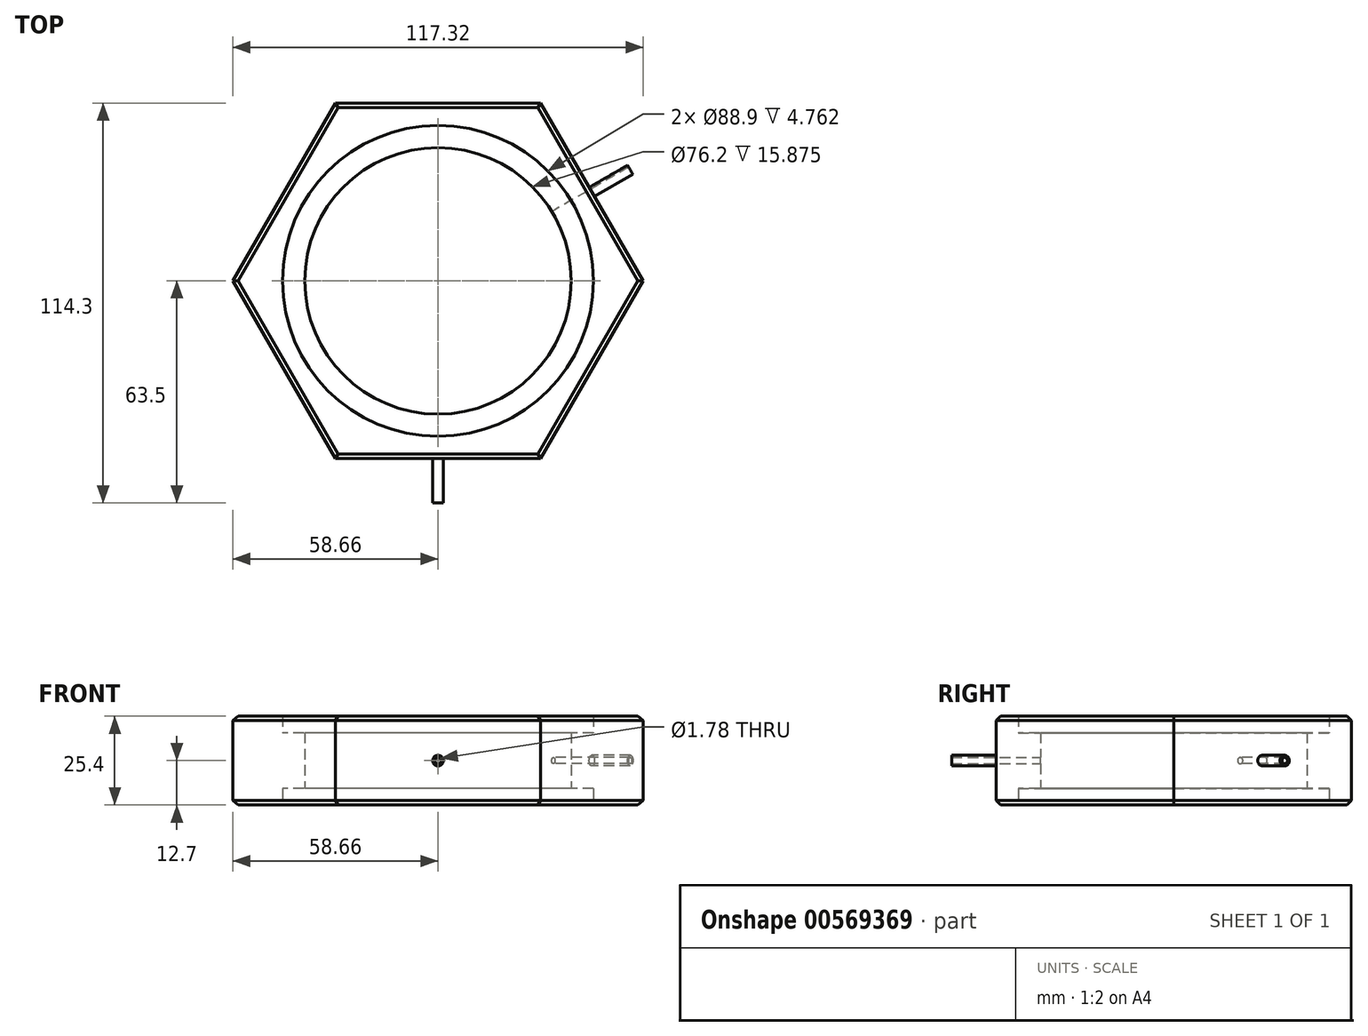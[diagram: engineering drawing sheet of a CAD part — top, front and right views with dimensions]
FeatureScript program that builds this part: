
annotation { "Feature Type Name" : "Feature", "Feature Type Description" : "" }
export const myFeature = defineFeature(function(context is Context, id is Id, definition is map)
    precondition{}
    {
        {
            var Q0;
            Q0=qCreatedBy(makeId("Top.planeOp"),FACE);
            var sketch = newSketch(context, id + "F0", { "sketchPlane" : qUnion([Q0])});
            skCircle(sketch, "E0.cCircle", {"center": v(0, 0) * mm, "radius": 50.8 * mm, "construction": true});
            skLineSegment(sketch, "E0.0", {"start": v(29.33, -50.8) * mm, "end": v(-29.33, -50.8) * mm});
            skLineSegment(sketch, "E0.1", {"start": v(-29.33, -50.8) * mm, "end": v(-58.66, 0) * mm});
            skLineSegment(sketch, "E0.2", {"start": v(-58.66, 0) * mm, "end": v(-29.33, 50.8) * mm});
            skLineSegment(sketch, "E0.3", {"start": v(-29.33, 50.8) * mm, "end": v(29.33, 50.8) * mm});
            skLineSegment(sketch, "E0.4", {"start": v(29.33, 50.8) * mm, "end": v(58.66, 0) * mm});
            skLineSegment(sketch, "E0.5", {"start": v(58.66, 0) * mm, "end": v(29.33, -50.8) * mm});
            skPoint(sketch, "E0.0.midPoint", {"position": v(0, -50.8) * mm});
            skCircle(sketch, "E1", {"center": v(0, 0) * mm, "radius": 44.45 * mm});
            skCircle(sketch, "E2", {"center": v(0, 0) * mm, "radius": 38.1 * mm});
            skPoint(sketch, "E3", {"position": v(0, 50.8) * mm});
            skPoint(sketch, "E4", {"position": v(0, 38.1) * mm});
            skPoint(sketch, "E5", {"position": v(44, 25.4) * mm});
            skPoint(sketch, "E6", {"position": v(33, 19.05) * mm});
            skLineSegment(sketch, "E7", {"start": v(0, 50.8) * mm, "end": v(1.28, 50.8) * mm});
            skLineSegment(sketch, "E8", {"start": v(44, 25.4) * mm, "end": v(44.63, 24.3) * mm});
            skLineSegment(sketch, "E9", {"start": v(44, 25.4) * mm, "end": v(33, 19.05) * mm});
            skLineSegment(sketch, "E10", {"start": v(0, 50.8) * mm, "end": v(0, 38.1) * mm});
            skSolve(sketch);
        }
        {
            var Q0;
            Q0 = qSketchRegion(id + "F0", true);
            extrude(context, id + "F1", {"entities" : qUnion([Q0]), "endBound" : BoundingType.SYMMETRIC, "depth" : 25.4 * mm, "offsetDistance" : 25.4 * mm});
        }
        {
            var Q0;
            Q0=makeQuery(id+"F0.imprint","IMPRINT",FACE,{"disambiguationData":[TD([[makeQuery(id+"F0.imprint","IMPRINT",EDGE,{"derivedFrom":sQuery(id+"F0.wireOp",EDGE,"E1")}),1.0]])]});
            extrude(context, id + "F2", {"entities" : qUnion([Q0]), "operationType" : NewBodyOperationType.ADD, "endBound" : BoundingType.SYMMETRIC, "depth" : 15.88 * mm, "offsetDistance" : 25.4 * mm});
        }
        {
            var Q0;
            Q0=makeQuery(id+"F1.opExtrude","CAP_EDGE",EDGE,{"disambiguationData":[OSD([sQuery(id+"F0.wireOp",EDGE,"E0.1")])],"isStart":false});
            var Q1;
            Q1=makeQuery(id+"F1.opExtrude","CAP_EDGE",EDGE,{"disambiguationData":[OSD([sQuery(id+"F0.wireOp",EDGE,"E0.0")])],"isStart":false});
            var Q2;
            Q2=makeQuery(id+"F1.opExtrude","CAP_EDGE",EDGE,{"disambiguationData":[OSD([sQuery(id+"F0.wireOp",EDGE,"E0.5")])],"isStart":false});
            var Q3;
            Q3=makeQuery(id+"F1.opExtrude","CAP_EDGE",EDGE,{"disambiguationData":[OSD([sQuery(id+"F0.wireOp",EDGE,"E0.4")])],"isStart":false});
            var Q4;
            Q4=makeQuery(id+"F1.opExtrude","CAP_EDGE",EDGE,{"disambiguationData":[OSD([sQuery(id+"F0.wireOp",EDGE,"E0.3")])],"isStart":false});
            var Q5;
            Q5=makeQuery(id+"F1.opExtrude","CAP_EDGE",EDGE,{"disambiguationData":[OSD([sQuery(id+"F0.wireOp",EDGE,"E0.2")])],"isStart":false});
            var Q6;
            Q6=makeQuery(id+"F1.opExtrude","CAP_EDGE",EDGE,{"disambiguationData":[OSD([sQuery(id+"F0.wireOp",EDGE,"E0.0")])],"isStart":true});
            var Q7;
            Q7=makeQuery(id+"F1.opExtrude","CAP_EDGE",EDGE,{"disambiguationData":[OSD([sQuery(id+"F0.wireOp",EDGE,"E0.5")])],"isStart":true});
            var Q8;
            Q8=makeQuery(id+"F1.opExtrude","CAP_EDGE",EDGE,{"disambiguationData":[OSD([sQuery(id+"F0.wireOp",EDGE,"E0.1")])],"isStart":true});
            var Q9;
            Q9=makeQuery(id+"F1.opExtrude","CAP_EDGE",EDGE,{"disambiguationData":[OSD([sQuery(id+"F0.wireOp",EDGE,"E0.4")])],"isStart":true});
            var Q10;
            Q10=makeQuery(id+"F1.opExtrude","CAP_EDGE",EDGE,{"disambiguationData":[OSD([sQuery(id+"F0.wireOp",EDGE,"E0.3")])],"isStart":true});
            var Q11;
            Q11=makeQuery(id+"F1.opExtrude","CAP_EDGE",EDGE,{"disambiguationData":[OSD([sQuery(id+"F0.wireOp",EDGE,"E0.2")])],"isStart":true});
            chamfer(context, id + "F3", {"entities" : qUnion([Q0, Q1, Q2, Q3, Q4, Q5, Q6, Q7, Q8, Q9, Q10, Q11]), "width" : 1.27 * mm, "tangentPropagation" : true});
        }
        {
            var Q0;
            Q0=makeQuery(id+"F1.opExtrude","SWEPT_FACE",FACE,{"disambiguationData":[OSD([sQuery(id+"F0.wireOp",EDGE,"E0.0")])]});
            var sketch = newSketch(context, id + "F4", { "sketchPlane" : qUnion([Q0])});
            skCircle(sketch, "E11", {"center": v(0, 0) * mm, "radius": 1.52 * mm});
            skCircle(sketch, "E12", {"center": v(0, 0) * mm, "radius": 0.89 * mm});
            skSolve(sketch);
        }
        {
            var Q0;
            Q0=makeQuery(id+"F4.imprint","IMPRINT",FACE,{"disambiguationData":[TD([[makeQuery(id+"F4.imprint","IMPRINT",EDGE,{"derivedFrom":sQuery(id+"F4.wireOp",EDGE,"E11")}),1.0]])]});
            extrude(context, id + "F5", {"entities" : qUnion([Q0]), "operationType" : NewBodyOperationType.ADD, "depth" : 12.7 * mm, "offsetDistance" : 25.4 * mm});
        }
        {
            var Q0;
            Q0=makeQuery(id+"F4.imprint","IMPRINT",FACE,{"disambiguationData":[TD([[makeQuery(id+"F4.imprint","IMPRINT",EDGE,{"derivedFrom":sQuery(id+"F4.wireOp",EDGE,"E12")}),1.0]])]});
            extrude(context, id + "F6", {"entities" : qUnion([Q0]), "operationType" : NewBodyOperationType.REMOVE, "endBound" : BoundingType.SYMMETRIC, "oppositeDirection" : true, "depth" : 50.8 * mm, "offsetDistance" : 25.4 * mm});
        }
        {
            var Q0;
            Q0=makeQuery(id+"F1.opExtrude","SWEPT_FACE",FACE,{"disambiguationData":[OSD([sQuery(id+"F0.wireOp",EDGE,"E0.4"),sQuery(id+"F0.wireOp",EDGE,"E8")])]});
            var sketch = newSketch(context, id + "F7", { "sketchPlane" : qUnion([Q0])});
            skCircle(sketch, "E13", {"center": v(0, 0) * mm, "radius": 1.52 * mm});
            skCircle(sketch, "E14", {"center": v(0, 0) * mm, "radius": 0.89 * mm});
            skSolve(sketch);
        }
        {
            var Q0;
            Q0=makeQuery(id+"F7.imprint","IMPRINT",FACE,{"disambiguationData":[TD([[makeQuery(id+"F7.imprint","IMPRINT",EDGE,{"derivedFrom":sQuery(id+"F7.wireOp",EDGE,"E13")}),1.0]])]});
            extrude(context, id + "F8", {"entities" : qUnion([Q0]), "operationType" : NewBodyOperationType.ADD, "depth" : 12.7 * mm, "offsetDistance" : 25.4 * mm});
        }
        {
            var Q0;
            Q0=makeQuery(id+"F8.boolean.opBoolean","SPLIT",FACE,{"disambiguationData":[TD([makeQuery(id+"F8.opExtrude","SWEPT_FACE",FACE,{"disambiguationData":[OSD([sQuery(id+"F7.wireOp",EDGE,"E14")])]})])],"derivedFrom":makeQuery(id+"F1.opExtrude","SWEPT_FACE",FACE,{"disambiguationData":[OSD([sQuery(id+"F0.wireOp",EDGE,"E0.4"),sQuery(id+"F0.wireOp",EDGE,"E8")])]})});
            extrude(context, id + "F9", {"entities" : qUnion([Q0]), "operationType" : NewBodyOperationType.REMOVE, "endBound" : BoundingType.SYMMETRIC, "oppositeDirection" : true, "depth" : 50.8 * mm, "offsetDistance" : 25.4 * mm});
        }
    });
